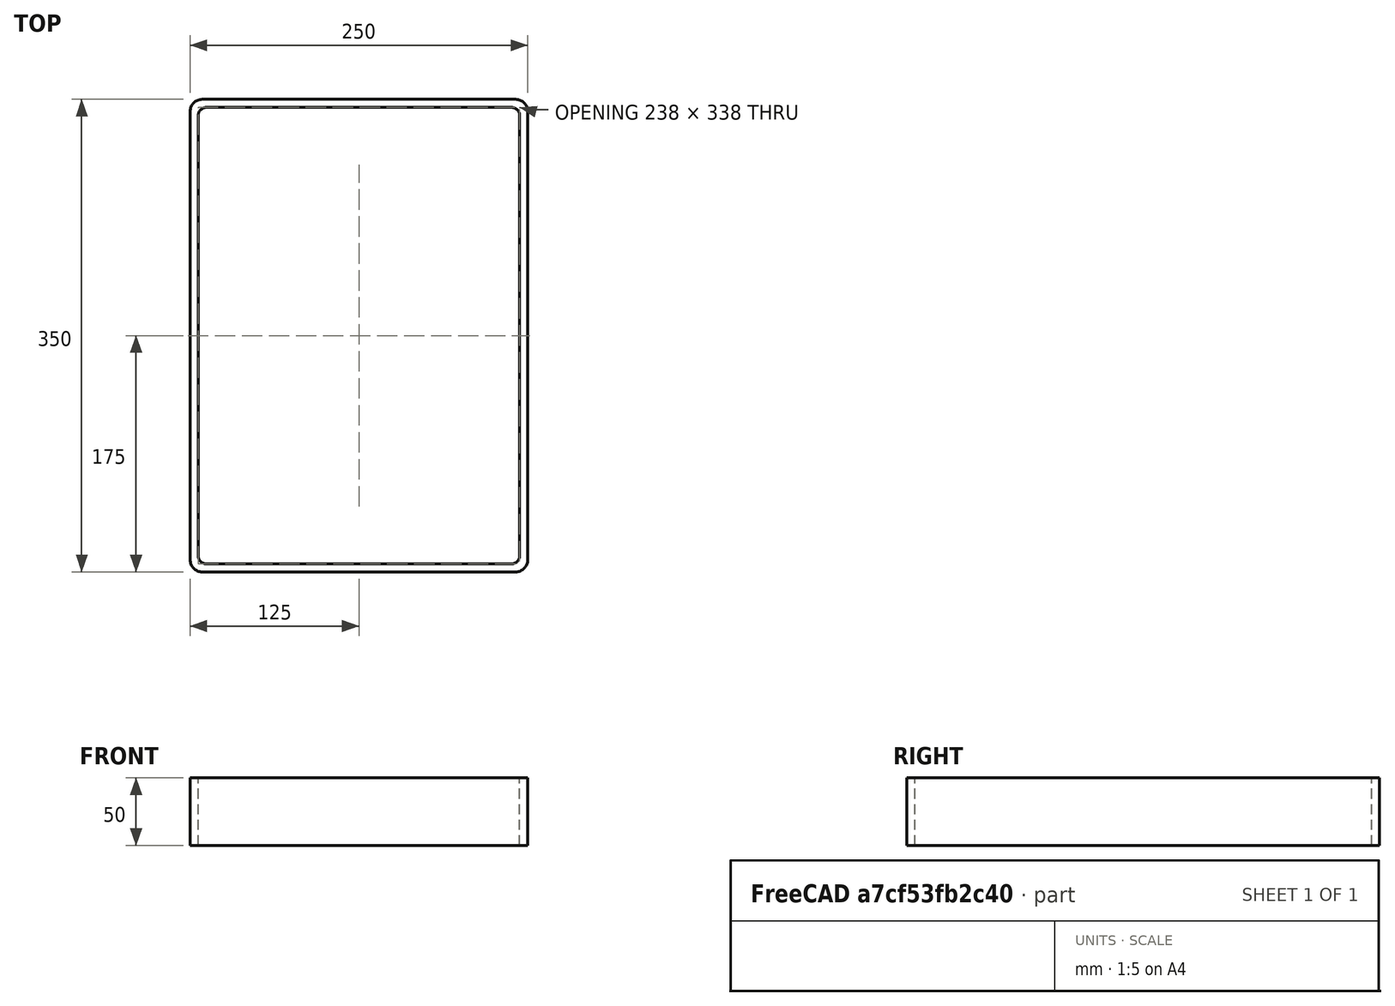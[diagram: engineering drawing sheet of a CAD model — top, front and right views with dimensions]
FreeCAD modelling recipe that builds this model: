
FCSTD DOCUMENT  (FreeCAD 0.15R4671 (Git))
Label: Rectangular hollow section 350x250x6 EN10219 S235JRH
License: All rights reserved
LicenseURL: http://en.wikipedia.org/wiki/All_rights_reserved
objects: Sketcher::SketchObject×1, Part::Extrusion×1
note: 2 computed .brp shape members not serialized (recipe doc carries the construction recipe); baked Part::Feature solids carry a one-line shape summary decoded from their .brp

FEATURE [Sketcher::SketchObject] Sketch
  sketch-geometry (16):
    g0: LineSegment StartX=-113 StartY=169 StartZ=0 EndX=113 EndY=169 EndZ=0
    g1: LineSegment StartX=119 StartY=163 StartZ=0 EndX=119 EndY=-163 EndZ=0
    g2: LineSegment StartX=113 StartY=-169 StartZ=0 EndX=-113 EndY=-169 EndZ=0
    g3: LineSegment StartX=-119 StartY=-163 StartZ=0 EndX=-119 EndY=163 EndZ=0
    g4: LineSegment StartX=-116 StartY=175 StartZ=0 EndX=116 EndY=175 EndZ=0
    g5: LineSegment StartX=125 StartY=166 StartZ=0 EndX=125 EndY=-166 EndZ=0
    g6: LineSegment StartX=116 StartY=-175 StartZ=0 EndX=-116 EndY=-175 EndZ=0
    g7: LineSegment StartX=-125 StartY=-166 StartZ=0 EndX=-125 EndY=166 EndZ=0
    g8: ArcOfCircle CenterX=-113 CenterY=163 CenterZ=0 NormalX=0 NormalY=0 NormalZ=1 Radius=6 StartAngle=1.5708 EndAngle=3.14159
    g9: ArcOfCircle CenterX=113 CenterY=163 CenterZ=0 NormalX=0 NormalY=0 NormalZ=1 Radius=6 StartAngle=0 EndAngle=1.5708
    g10: ArcOfCircle CenterX=113 CenterY=-163 CenterZ=0 NormalX=0 NormalY=0 NormalZ=1 Radius=6 StartAngle=4.71239 EndAngle=6.28319
    g11: ArcOfCircle CenterX=-113 CenterY=-163 CenterZ=0 NormalX=0 NormalY=0 NormalZ=1 Radius=6 StartAngle=3.14159 EndAngle=4.71239
    g12: ArcOfCircle CenterX=116 CenterY=166 CenterZ=0 NormalX=0 NormalY=0 NormalZ=1 Radius=9 StartAngle=0 EndAngle=1.5708
    g13: ArcOfCircle CenterX=116 CenterY=-166 CenterZ=0 NormalX=0 NormalY=0 NormalZ=1 Radius=9 StartAngle=4.71239 EndAngle=6.28319
    g14: ArcOfCircle CenterX=-116 CenterY=-166 CenterZ=0 NormalX=0 NormalY=0 NormalZ=1 Radius=9 StartAngle=3.14159 EndAngle=4.71239
    g15: ArcOfCircle CenterX=-116 CenterY=166 CenterZ=0 NormalX=0 NormalY=0 NormalZ=1 Radius=9 StartAngle=1.5708 EndAngle=3.14159
  constraints (36):
    c: Horizontal(g2)
    c: Vertical(g3)
    c: Horizontal(g6)
    c: Vertical(g7)
    c: Tangent(g3,g8) = 1.5708
    c: Tangent(g0,g8) = 1.5708
    c: Tangent(g0,g9) = 1.5708
    c: Tangent(g1,g9) = 1.5708
    c: Tangent(g1,g10) = 1.5708
    c: Tangent(g2,g10) = 1.5708
    c: Tangent(g2,g11) = 1.5708
    c: Tangent(g3,g11) = 1.5708
    c: Tangent(g4,g12) = 1.5708
    c: Tangent(g5,g12) = 1.5708
    c: Tangent(g5,g13) = 1.5708
    c: Tangent(g6,g13) = 1.5708
    c: Tangent(g6,g14) = 1.5708
    c: Tangent(g7,g14) = 1.5708
    c: Tangent(g7,g15) = 1.5708
    c: Tangent(g4,g15) = 1.5708
    c: Equal(g9,g8)
    c: Equal(g9,g11)
    c: Equal(g9,g10)
    c: Equal(g12,g15)
    c: Equal(g12,g14)
    c: Equal(g12,g13)
    c: Symmetric(g4,g6,g-1)
    c: Symmetric(g7,g5,g-2)
    c: DistanceY(g4,g6) = -350
    c: DistanceX(g7,g5) = 250
    c: Symmetric(g3,g1,g-2)
    c: Symmetric(g0,g2,g-1)
    c: DistanceY(g0,g4) = 6
    c: DistanceX(g5,g1) = -6
    c: Radius(g9) = 6
    c: Radius(g12) = 9
FEATURE [Part::Extrusion] Extrude  label="Rectangular hollow section 350x250x6 EN10219 S235JRH"
  Base = -> Sketch
  Dir = (0,0,50)
  Solid = true
